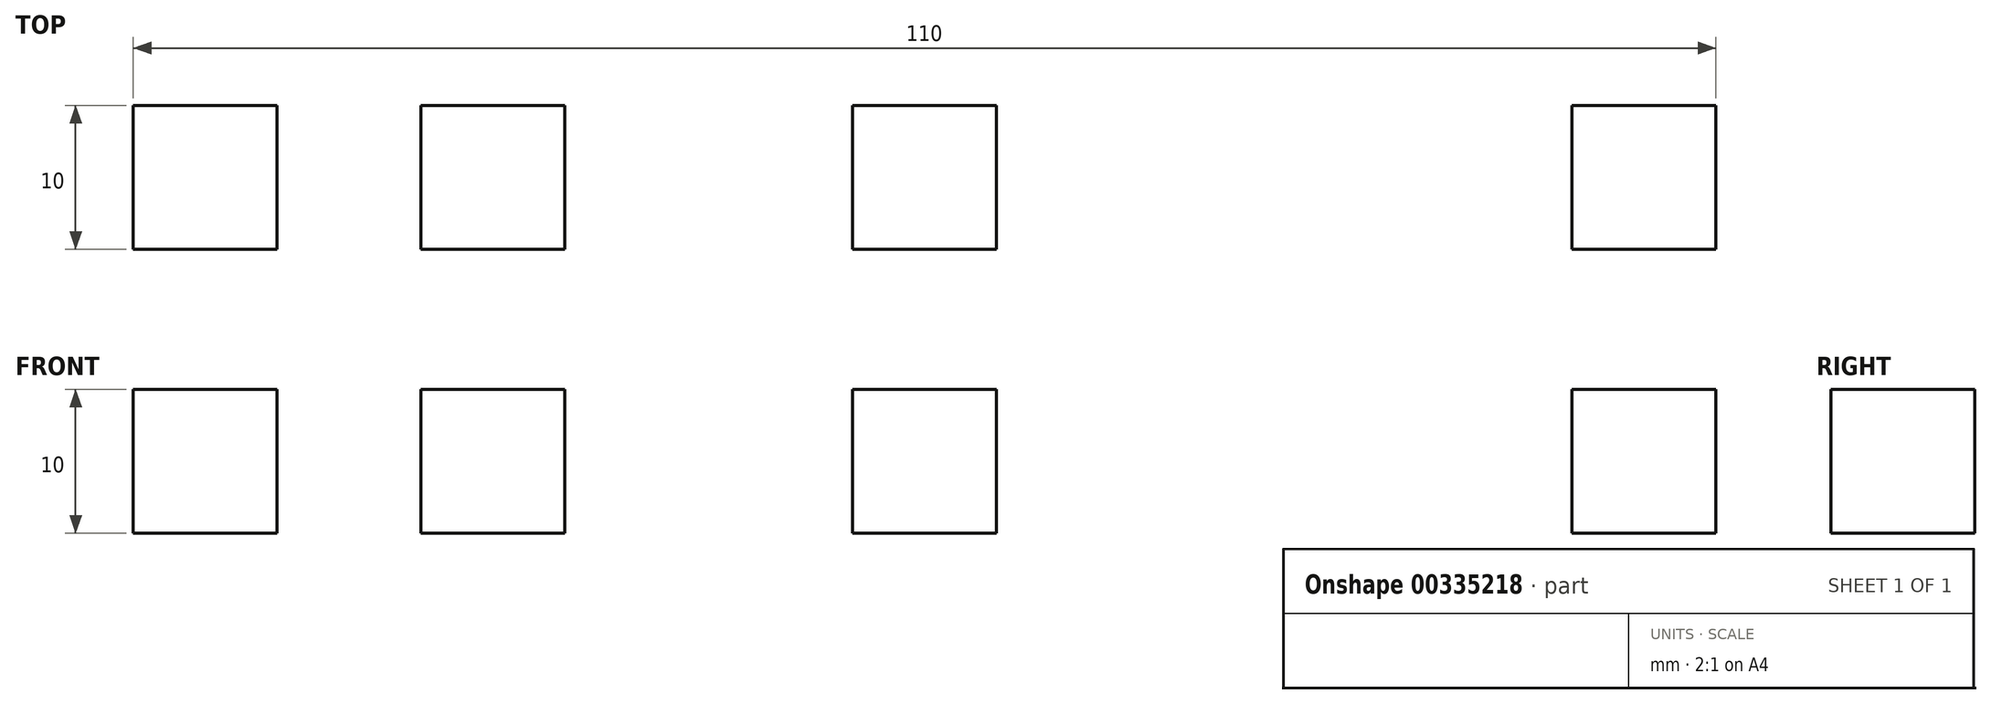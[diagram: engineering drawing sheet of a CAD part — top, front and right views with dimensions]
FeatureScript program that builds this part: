
annotation { "Feature Type Name" : "Feature", "Feature Type Description" : "" }
export const myFeature = defineFeature(function(context is Context, id is Id, definition is map)
    precondition{}
    {
        {
            var Q0;
            Q0=qCreatedBy(makeId("Top.planeOp"),FACE);
            var sketch = newSketch(context, id + "F0", { "sketchPlane" : qUnion([Q0])});
            skLineSegment(sketch, "E0.bottom", {"start": v(-45, 5) * mm, "end": v(-55, 5) * mm});
            skLineSegment(sketch, "E0.top", {"start": v(-45, -5) * mm, "end": v(-55, -5) * mm});
            skLineSegment(sketch, "E0.left", {"start": v(-45, 5) * mm, "end": v(-45, -5) * mm});
            skLineSegment(sketch, "E0.right", {"start": v(-55, 5) * mm, "end": v(-55, -5) * mm});
            skPoint(sketch, "E0.middle", {"position": v(-50, 0) * mm});
            skLineSegment(sketch, "E1.bottom", {"start": v(-25, 5) * mm, "end": v(-35, 5) * mm});
            skLineSegment(sketch, "E1.top", {"start": v(-25, -5) * mm, "end": v(-35, -5) * mm});
            skLineSegment(sketch, "E1.left", {"start": v(-25, 5) * mm, "end": v(-25, -5) * mm});
            skLineSegment(sketch, "E1.right", {"start": v(-35, 5) * mm, "end": v(-35, -5) * mm});
            skPoint(sketch, "E1.middle", {"position": v(-30, 0) * mm});
            skLineSegment(sketch, "E2.bottom", {"start": v(5, 5) * mm, "end": v(-5, 5) * mm});
            skLineSegment(sketch, "E2.top", {"start": v(5, -5) * mm, "end": v(-5, -5) * mm});
            skLineSegment(sketch, "E2.left", {"start": v(5, 5) * mm, "end": v(5, -5) * mm});
            skLineSegment(sketch, "E2.right", {"start": v(-5, 5) * mm, "end": v(-5, -5) * mm});
            skPoint(sketch, "E2.middle", {"position": v(0, 0) * mm});
            skLineSegment(sketch, "E3.bottom", {"start": v(55, 5) * mm, "end": v(45, 5) * mm});
            skLineSegment(sketch, "E3.top", {"start": v(55, -5) * mm, "end": v(45, -5) * mm});
            skLineSegment(sketch, "E3.left", {"start": v(55, 5) * mm, "end": v(55, -5) * mm});
            skLineSegment(sketch, "E3.right", {"start": v(45, 5) * mm, "end": v(45, -5) * mm});
            skPoint(sketch, "E3.middle", {"position": v(50, 0) * mm});
            skSolve(sketch);
        }
        {
            var Q0;
            Q0=makeQuery(id+"F0.imprint","IMPRINT",FACE,{"disambiguationData":[TD([[makeQuery(id+"F0.imprint","IMPRINT",EDGE,{"derivedFrom":sQuery(id+"F0.wireOp",EDGE,"E0.bottom")}),1.0]])]});
            var Q1;
            Q1=makeQuery(id+"F0.imprint","IMPRINT",FACE,{"disambiguationData":[TD([[makeQuery(id+"F0.imprint","IMPRINT",EDGE,{"derivedFrom":sQuery(id+"F0.wireOp",EDGE,"E1.bottom")}),1.0]])]});
            var Q2;
            Q2=makeQuery(id+"F0.imprint","IMPRINT",FACE,{"disambiguationData":[TD([[makeQuery(id+"F0.imprint","IMPRINT",EDGE,{"derivedFrom":sQuery(id+"F0.wireOp",EDGE,"E2.bottom")}),1.0]])]});
            var Q3;
            Q3=makeQuery(id+"F0.imprint","IMPRINT",FACE,{"disambiguationData":[TD([[makeQuery(id+"F0.imprint","IMPRINT",EDGE,{"derivedFrom":sQuery(id+"F0.wireOp",EDGE,"E3.bottom")}),1.0]])]});
            extrude(context, id + "F1", {"entities" : qUnion([Q0, Q1, Q2, Q3]), "depth" : 10 * mm});
        }
    });
